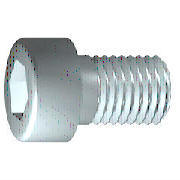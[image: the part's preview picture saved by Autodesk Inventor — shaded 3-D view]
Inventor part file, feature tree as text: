
AUTODESK INVENTOR PART (.ipt)
format: ipt  version: 2018 (Build 220112000, 112)  size: 184,320 bytes
history: native  units: mm (DEFAULTED — no unit token found)
features: sketch x2, extrude x1, plane x1, fillet x1
ambient origin geometry x7: Origin, YZ Plane, XY Plane, X Axis, Y Axis, Z Axis, Center Point
bodies: Solid1 (feature_tree), Body (feature_tree)
feature tree (5):
  extrude  "Slot"  Depth=3.0mm
  plane  "Work Plane1"
  fillet  "Fillet2"  Radius=3.0mm
  sketch  "Sketch1"  dims[d1=18.0mm d2=0.306825mm d3=3.0mm]
  sketch  "Sketch2"  dims[d4=1.5mm d5=60.0deg d6=3.0mm d7=3.0mm d8=2.886751mm d9=5.5mm d10=90.0deg d11=10.0mm d12=0.0mm d13=18.0mm d14=0.0mm d15=0.306725mm d16=0.306725mm d17=0.3mm d19=0.0mm d26=25.0mm d27=45.0deg d28=0.0mm d29=0.0mm d30=0.1mm]
